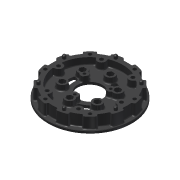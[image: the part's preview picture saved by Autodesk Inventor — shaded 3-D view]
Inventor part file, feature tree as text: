
AUTODESK INVENTOR PART (.ipt)
format: ipt  version: 2015 (Build 190159000, 159)  size: 1,575,936 bytes
history: native  units: in
note: dims shown in document units (in); Inventor stores cm internally (conversion verified against a paired STEP export)
features: fillet x1, other x1, imported_body x1
ambient origin geometry x8: Origin, YZ Plane, XZ Plane, XY Plane, X Axis, Y Axis, Z Axis, Center Point
bodies: Body1 (feature_tree)
feature tree (3):
  fillet  "Fillet18"  [1 undecoded]
  other  "217-2588-001 Rev41"
  imported_body  "Base1"
note: 1 required parameter value undecoded (feature->parameter linkage not recoverable at this tier; creation-order binding heuristic only, values carry confidence <= 0.55)
